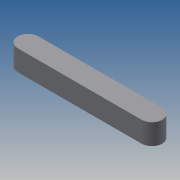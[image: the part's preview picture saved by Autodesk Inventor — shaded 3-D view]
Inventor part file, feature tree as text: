
AUTODESK INVENTOR PART (.ipt)
format: ipt  version: 2013 (Build 170138000, 138)  size: 68,608 bytes
history: native  units: mm
features: extrude x1, sketch x1
ambient origin geometry x8: Origin, YZ Plane, XZ Plane, XY Plane, X Axis, Y Axis, Z Axis, Center Point
bodies: Solid1 (feature_tree)
feature tree (2):
  extrude  "Extrusion1"  Depth=12.5mm
  sketch  "Sketch1"  dims[d0=150.0mm d2=12.5mm d3=25.0mm d4=0.0mm]
